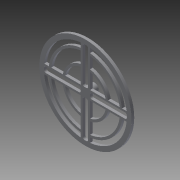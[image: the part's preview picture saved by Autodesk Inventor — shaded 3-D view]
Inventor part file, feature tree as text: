
AUTODESK INVENTOR PART (.ipt)
format: ipt  version: 2015 (Build 190159000, 159)  size: 237,056 bytes
history: native  units: mm
features: sketch x6, extrude x5, fillet x2
ambient origin geometry x8: Origin, YZ Plane, XZ Plane, XY Plane, X Axis, Y Axis, Z Axis, Center Point
bodies: Solid1 (feature_tree)
feature tree (13):
  extrude  "Extrusion1"  Depth=90.0mm
  extrude  "Extrusion2"  Depth=5.0mm
  extrude  "Extrusion3"  Depth=5.0mm
  sketch  "Sketch4"  dims[d6=3.0mm d7=0.0mm d8=80.0mm]
  extrude  "Extrusion4"  Depth=3.0mm
  extrude  "Extrusion5"  Depth=50.0mm
  fillet  "Fillet1"  Radius=45.0mm
  fillet  "Fillet2"  Radius=3.0mm
  sketch  "Sketch1"  dims[d0=100.0mm d1=90.0mm]
  sketch  "Sketch2"  dims[d2=5.0mm d3=5.0mm]
  sketch  "Sketch3"  dims[d4=5.0mm d5=5.0mm]
  sketch  "Sketch5"  dims[d9=75.0mm d10=50.0mm d11=45.0mm d12=3.0mm d13=0.0mm]
  sketch  "Sketch6"  dims[d14=9.0mm d15=6.2mm d16=3.2mm d17=1.51mm d18=3.1mm d19=7.0mm d20=0.0mm d21=90.0mm d22=90.0mm d23=45.0mm d24=45.0mm d25=3.0mm d26=3.0mm d27=3.0mm d28=3.0mm d29=3.0mm d30=0.0mm d31=3.0mm d32=0.0mm d33=2.0mm d34=2.0mm]
